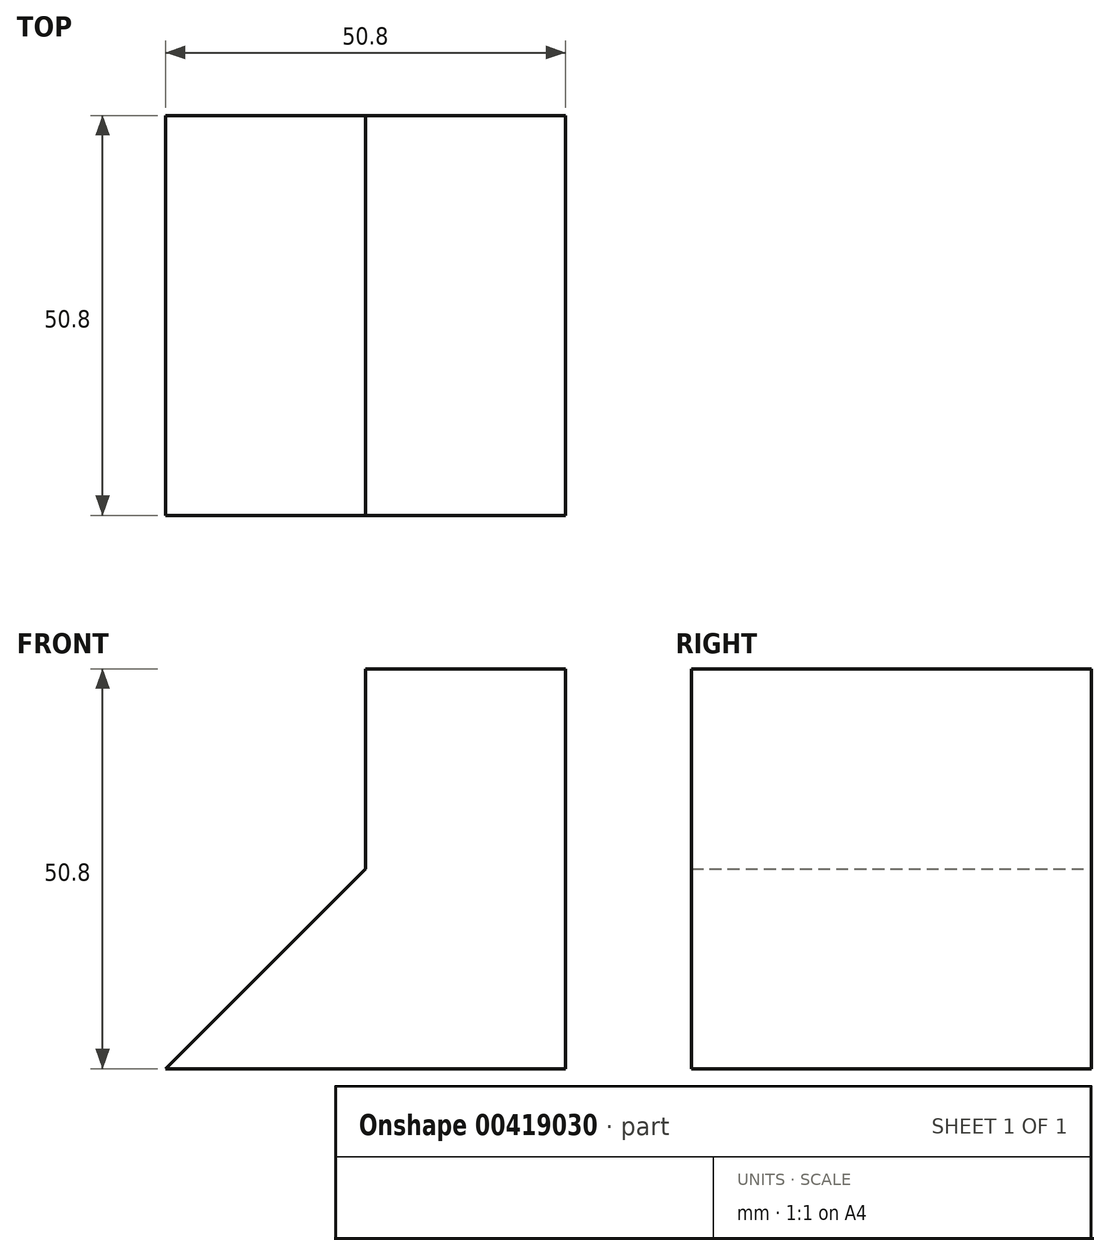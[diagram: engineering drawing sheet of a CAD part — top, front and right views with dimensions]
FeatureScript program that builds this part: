
annotation { "Feature Type Name" : "Feature", "Feature Type Description" : "" }
export const myFeature = defineFeature(function(context is Context, id is Id, definition is map)
    precondition{}
    {
        {
            var Q0;
            Q0=qCreatedBy(makeId("Front.planeOp"),FACE);
            var sketch = newSketch(context, id + "F0", { "sketchPlane" : qUnion([Q0])});
            skLineSegment(sketch, "E0", {"start": v(0, 0) * mm, "end": v(0, 50.8) * mm});
            skLineSegment(sketch, "E1", {"start": v(0, 50.8) * mm, "end": v(-25.4, 50.8) * mm});
            skLineSegment(sketch, "E2", {"start": v(-25.4, 50.8) * mm, "end": v(-25.4, 25.4) * mm});
            skLineSegment(sketch, "E3", {"start": v(0, 0) * mm, "end": v(-50.8, 0) * mm});
            skLineSegment(sketch, "E4", {"start": v(-50.8, 0) * mm, "end": v(-25.4, 25.4) * mm});
            skSolve(sketch);
        }
        {
            var Q0;
            Q0 = qSketchRegion(id + "F0", true);
            var Q1;
            Q1=makeQuery(id+"F0.imprint","IMPRINT",FACE,{"disambiguationData":[TD([[makeQuery(id+"F0.imprint","IMPRINT",EDGE,{"derivedFrom":sQuery(id+"F0.wireOp",EDGE,"E0")}),1.0]])]});
            extrude(context, id + "F1", {"entities" : qUnion([Q0, Q1]), "depth" : 50.8 * mm});
        }
    });
